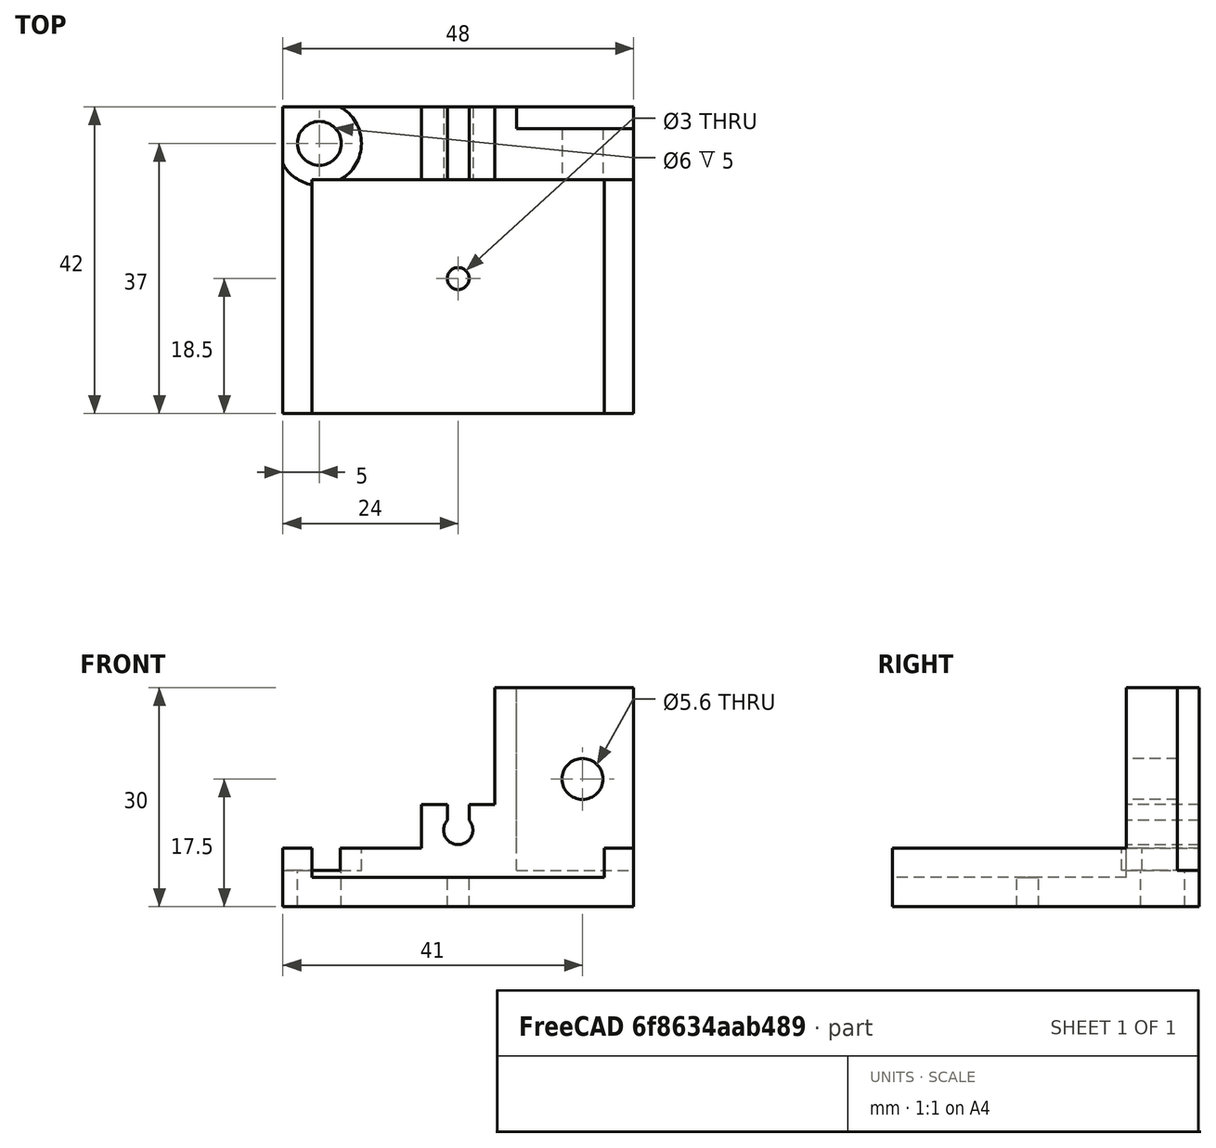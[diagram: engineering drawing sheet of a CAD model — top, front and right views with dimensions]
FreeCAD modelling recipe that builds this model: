
FCSTD DOCUMENT  (FreeCAD 0.19R24276 (Git))
Label: gpsold04132022
License: All rights reserved
LicenseURL: http://en.wikipedia.org/wiki/All_rights_reserved
objects: Part::Cylinder×6, Part::Box×6, Part::Cut×5, Part::MultiFuse×4
note: 21 computed .brp shape members not serialized (recipe doc carries the construction recipe); baked Part::Feature solids carry a one-line shape summary decoded from their .brp

FEATURE [Part::Cylinder] Cylinder011  label="Cylinder001"
  Angle = 360
  AttacherType = Attacher::AttachEngine3D
  Height = 20
  Placement = pos=(13.5,87,63.5) rot=(0,0.707107,0.707107;3.14159rad)
  Radius = 2
FEATURE [Part::Cylinder] Cylinder012  label="cut001"
  Angle = 360
  AttacherType = Attacher::AttachEngine3D
  Height = 42
  Placement = pos=(13.5,110.5,42.5) rot=(0,0,1;3.14159rad)
  Radius = 1.5
FEATURE [Part::Box] Box020  label="gpsCut"
  AttacherType = Attacher::AttachEngine3D
  Height = 40
  Length = 18
  Placement = pos=(33.5,97,57) rot=(0,-1,0;1.5708rad)
  Width = 50
FEATURE [Part::Box] Box018  label="shell"
  AttacherType = Attacher::AttachEngine3D
  Height = 48
  Length = 8
  Placement = pos=(37.5,87,53) rot=(0,-1,0;1.5708rad)
  Width = 42
FEATURE [Part::Box] Box021  label="shell003"
  AttacherType = Attacher::AttachEngine3D
  Height = 3
  Length = 9
  Placement = pos=(15,87,63) rot=(0,-1,0;1.5708rad)
  Width = 32
FEATURE [Part::Box] Box019  label="shell002"
  AttacherType = Attacher::AttachEngine3D
  Height = 10
  Length = 10
  Placement = pos=(18.5,87,57) rot=(0,-1,0;1.5708rad)
  Width = 10
FEATURE [Part::MultiFuse] Fusion
  Shapes = -> [Box019,Box018]
FEATURE [Part::MultiFuse] Fusion001
  Shapes = -> [Box021,Cylinder011,Cylinder012,Box020]
FEATURE [Part::Cut] Cut  label="gpsHoler"
  Base = -> Fusion
  Placement = pos=(0,0,0) rot=(0,0,1;3.14159rad)
  Tool = -> Fusion001
FEATURE [Part::Box] Box  label="cut"
  AttacherType = Attacher::AttachEngine3D
  Height = 16
  Length = 25
  Placement = pos=(10.5,-90,58) rot=(0,1,0;4.71239rad)
  Width = 10
FEATURE [Part::Box] Box022  label="addOn"
  AttacherType = Attacher::AttachEngine3D
  Height = 19
  Length = 30
  Placement = pos=(10.5,-97,53) rot=(0,-1,0;1.5708rad)
  Width = 10
FEATURE [Part::Cylinder] Cylinder
  Angle = 360
  AttacherType = Attacher::AttachEngine3D
  Height = 19
  Placement = pos=(3.5,-80,70.5) rot=(1,0,0;1.5708rad)
  Radius = 2.8
FEATURE [Part::MultiFuse] Fusion002
  Shapes = -> [Box,Cylinder]
FEATURE [Part::MultiFuse] Fusion003  label="gpsHolder"
  Shapes = -> [Box022,Cut]
FEATURE [Part::Cut] Cut001  label="gpsHolder001"
  Base = -> Fusion003
  Tool = -> Fusion002
FEATURE [Part::Cylinder] Cylinder013
  Angle = 360
  AttacherType = Attacher::AttachEngine3D
  Height = 10
  Placement = pos=(-32.5,-92,53) rot=(0,0,1;0rad)
  Radius = 3
FEATURE [Part::Cylinder] Cylinder014
  Angle = 360
  AttacherType = Attacher::AttachEngine3D
  Height = 10
  Placement = pos=(-32.5,-92,58) rot=(0,0,1;4.97419rad)
  Radius = 5.75
FEATURE [Part::Cut] Cut002
  Base = -> Cut001
  Tool = -> Cylinder013
FEATURE [Part::Cut] Cut003
  Base = -> Cut002
  Tool = -> Cylinder014
FEATURE [Part::Cylinder] Cylinder015
  Angle = 90
  AttacherType = Attacher::AttachEngine3D
  Height = 10
  Placement = pos=(-32.5,-92,58) rot=(0,0,-1;4.71239rad)
  Radius = 7.75
FEATURE [Part::Cut] Cut004  label="gpsHolder002"
  Base = -> Cut003
  Tool = -> Cylinder015
